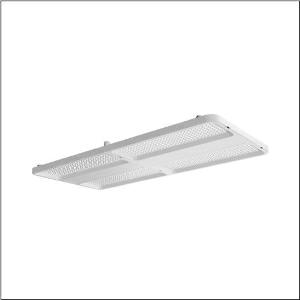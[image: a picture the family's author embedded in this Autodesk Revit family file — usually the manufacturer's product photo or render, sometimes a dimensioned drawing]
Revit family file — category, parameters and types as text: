
# Revit family: highbay_21_maxi_52hn12db4tea
name_source: partatom
category: Lighting Fixtures
units: mm (PartAtom-declared; Revit-internal decimal feet)

## family parameters
Cut with Voids When Loaded = No
Host = Face
Light Source = No
Part Type = Normal
Room Calculation Point = No
Round Connector Dimension = Use Diameter
Shared = No

## types (1)
- --- (1 x LED, 8350 lm, 44.8 W, 4000K)
    Apparent Load = 45 VA
    CIE Flux Codes = 90 98 100 100 100
    Color Rendering = 80
    Color Temperature = 4000K
    Default Elevation = 1800 mm
    Description = high bay luminaire Highbay 21 maxi; direct symmetric wide distribution, light control with lens of PMMA; UGR ≤ 22 (X = 4H | Y = 8H | S = 0.25H | reflection values 70/50/20); luminous flux: 53.000lm; light colour: 840, colour temperature: 4000K, MacAdam ≤ 3 SDCM (initial), colour rendering: CRI > 80; luminous efficacy: 184,9lm/W; rated service life: 75.000h (L80) at AT= ta max; control: DALI 2; luminaire connection: 2x terminal, 5-pole, max. 2.5mm² with through-wiring: 1x feed-in / 1x feed-out (cable entry for two cables, Ø 8.5..13mm); mains connection: 230..240V, AC/DC 0/50..60Hz; connected load: 286,6W; protection rating (complete): IP66; insulation class (complete): insulation class I (protective earthing); protection symbol: D; impact resistance: IK08; certification: CE, ENEC, VDE, UKCA; luminaire for central battery installations according to EN 60598-2-22, internal wiring halogen-free; luminaire LABS conformity tested according to VDMA 24364:2018-05; Suitable for use in the food industry according to the specifications of IFS-Food, HACCP and/or BRC; housing frame of high-performance plastic PA6, matt traffic white (RAL 9016); cover of PMMA; dimension (LxWxH): 946 x 442 x 72mm; permissible operating ambient temperature: -40..+55°C (reducing of maximum allowable ambient temperature of 5°C with ceiling mounting); packaging unit: 1 piece; (delivery without accessories; please order mounting accessories separately)
    Height = 72 mm  [stored 0.23622 ft]
    Lamp = 1 x LED
    Lamp Light Flux = 8350 lm
    Lamp Power = 44.8 W
    Lamp count = 1
    Length = 946 mm
    Luminous efficacy = 186 lm/W
    Manufacturer = Siteco
    ModVariant = No
    Model = 52HN12DB4TEA
    Mounting Place = Ceiling
    Mounting Type = Pendant
    Number of Poles = 1
    OnlyDefault = Yes
    Power Factor = 1
    Product Name = Highbay 21 maxi
    Product group = high bay luminaire
    ProductGroupID = 902
    Protection Class = Protection class I
    Protection Degree = IP 66
    RLX_Detail_Level = 1
    RLX_Emergency_Light_Flux = 0 lm
    RLX_Emergency_Type = 0
    RLX_Emergency_Type_DB = No
    RlxData = <blob elided: 128201 chars, md5=97ed234e>
    Socket = socket
    Standby Power = 0 W
    System Light Flux = 8350 lm
    System Power = 45 W
    Type Comments = : DC mode (central or group accumulator) initial emergency light level
    Type Image = l_1363244.jpg
    URL = http://relux.com
    VarID = @adj_019269
    Voltage = 0 V
    Weight = 0.00 kg
    Width = 442 mm

note: [stored X ft] marks values corroborated as IEEE doubles in the binary element streams (Revit-internal decimal feet)

## geometry (parser evidence)
native form markers: Blend x4, Sweep x10
no freeform markers — native parametric forms only
